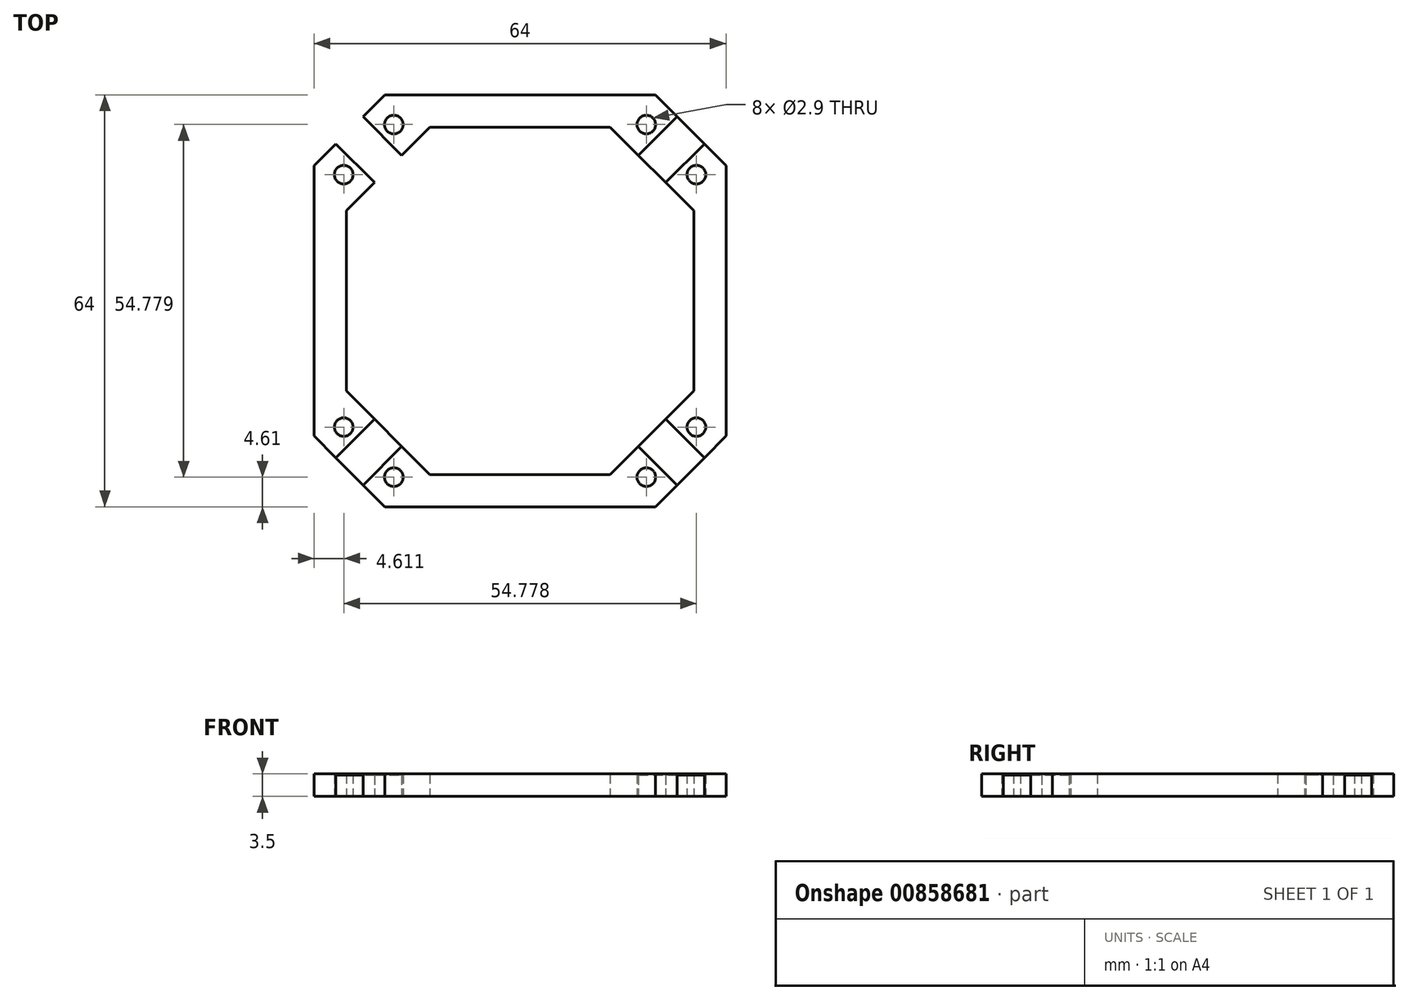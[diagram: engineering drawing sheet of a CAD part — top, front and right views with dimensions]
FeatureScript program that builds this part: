
annotation { "Feature Type Name" : "Feature", "Feature Type Description" : "" }
export const myFeature = defineFeature(function(context is Context, id is Id, definition is map)
    precondition{}
    {
        {
            var Q0;
            Q0=qCreatedBy(makeId("Top.planeOp"),FACE);
            var sketch = newSketch(context, id + "F0", { "sketchPlane" : qUnion([Q0])});
            skLineSegment(sketch, "E0.bottom", {"start": v(21, 32) * mm, "end": v(-21, 32) * mm});
            skLineSegment(sketch, "E0.top", {"start": v(21, -32) * mm, "end": v(-21, -32) * mm});
            skLineSegment(sketch, "E0.left", {"start": v(32, 21) * mm, "end": v(32, -21) * mm});
            skLineSegment(sketch, "E0.right", {"start": v(-32, 21) * mm, "end": v(-32, -21) * mm});
            skPoint(sketch, "E0.middle", {"position": v(0, 0) * mm});
            skLineSegment(sketch, "E1.left", {"start": v(27, 14) * mm, "end": v(27, -14) * mm});
            skLineSegment(sketch, "E1.right", {"start": v(-27, 14) * mm, "end": v(-27, -14) * mm});
            skLineSegment(sketch, "E2.bottom", {"start": v(14, 27) * mm, "end": v(-14, 27) * mm});
            skLineSegment(sketch, "E2.top", {"start": v(14, -27) * mm, "end": v(-14, -27) * mm});
            skLineSegment(sketch, "E3", {"start": v(-27, 14) * mm, "end": v(-14, 27) * mm});
            skLineSegment(sketch, "E4", {"start": v(14, 27) * mm, "end": v(27, 14) * mm});
            skLineSegment(sketch, "E5", {"start": v(-27, -14) * mm, "end": v(-14, -27) * mm});
            skLineSegment(sketch, "E6", {"start": v(14, -27) * mm, "end": v(27, -14) * mm});
            skLineSegment(sketch, "E7", {"start": v(-32, 21) * mm, "end": v(-21, 32) * mm});
            skLineSegment(sketch, "E8", {"start": v(-32, -21) * mm, "end": v(-21, -32) * mm});
            skLineSegment(sketch, "E9", {"start": v(21, -32) * mm, "end": v(32, -21) * mm});
            skLineSegment(sketch, "E10", {"start": v(21, 32) * mm, "end": v(32, 21) * mm});
            skLineSegment(sketch, "E11", {"start": v(-32, 21) * mm, "end": v(-28.06, 24.94) * mm});
            skLineSegment(sketch, "E12", {"start": v(-25.62, 21.38) * mm, "end": v(-28.62, 24.38) * mm});
            skLineSegment(sketch, "E13", {"start": v(-28.62, 24.38) * mm, "end": v(-25.62, 21.38) * mm});
            skLineSegment(sketch, "E14", {"start": v(-25.62, 21.38) * mm, "end": v(-22.62, 18.38) * mm});
            skLineSegment(sketch, "E15", {"start": v(-21.38, 25.62) * mm, "end": v(-24.38, 28.62) * mm});
            skLineSegment(sketch, "E16", {"start": v(-24.38, 28.62) * mm, "end": v(-21.38, 25.62) * mm});
            skLineSegment(sketch, "E17", {"start": v(-21.38, 25.62) * mm, "end": v(-18.38, 22.62) * mm});
            skLineSegment(sketch, "E18", {"start": v(21.88, 26.13) * mm, "end": v(18.38, 22.62) * mm});
            skLineSegment(sketch, "E19", {"start": v(18.38, 22.62) * mm, "end": v(24.38, 28.62) * mm});
            skLineSegment(sketch, "E20", {"start": v(25.62, 21.38) * mm, "end": v(22.62, 18.38) * mm});
            skLineSegment(sketch, "E21", {"start": v(22.62, 18.38) * mm, "end": v(28.62, 24.38) * mm});
            skLineSegment(sketch, "E22", {"start": v(-25.62, -21.38) * mm, "end": v(-28.62, -24.38) * mm});
            skLineSegment(sketch, "E23", {"start": v(-28.62, -24.38) * mm, "end": v(-22.62, -18.38) * mm});
            skLineSegment(sketch, "E24", {"start": v(-21.76, -26) * mm, "end": v(-24.38, -28.62) * mm});
            skLineSegment(sketch, "E25", {"start": v(-24.38, -28.62) * mm, "end": v(-18.38, -22.62) * mm});
            skLineSegment(sketch, "E26", {"start": v(20.86, -25.1) * mm, "end": v(18.38, -22.62) * mm});
            skLineSegment(sketch, "E27", {"start": v(18.38, -22.62) * mm, "end": v(24.38, -28.62) * mm});
            skLineSegment(sketch, "E28", {"start": v(25.62, -21.38) * mm, "end": v(22.62, -18.38) * mm});
            skLineSegment(sketch, "E29", {"start": v(22.62, -18.38) * mm, "end": v(28.62, -24.38) * mm});
            skCircle(sketch, "E30", {"center": v(-27.39, 19.61) * mm, "radius": 1.45 * mm});
            skCircle(sketch, "E31", {"center": v(-19.61, 27.39) * mm, "radius": 1.45 * mm});
            skCircle(sketch, "E32", {"center": v(19.61, 27.39) * mm, "radius": 1.45 * mm});
            skCircle(sketch, "E33", {"center": v(27.39, 19.61) * mm, "radius": 1.45 * mm});
            skCircle(sketch, "E34", {"center": v(-27.39, -19.61) * mm, "radius": 1.45 * mm});
            skCircle(sketch, "E35", {"center": v(-19.61, -27.39) * mm, "radius": 1.45 * mm});
            skCircle(sketch, "E36", {"center": v(19.61, -27.39) * mm, "radius": 1.45 * mm});
            skCircle(sketch, "E37", {"center": v(27.39, -19.61) * mm, "radius": 1.45 * mm});
            skSolve(sketch);
        }
        {
            var Q0;
            {var subQ0=sQuery(id+"F0.wireOp",EDGE,"E13");Q0=makeQuery(id+"F0.imprint","IMPRINT",FACE,{"disambiguationData":[TD([[makeQuery(id+"F0.imprint","IMPRINT",EDGE,{"derivedFrom":subQ0}),1.0]])]});}
            var Q1;
            {var subQ0=sQuery(id+"F0.wireOp",EDGE,"E19");var subQ3=makeQuery(id+"F0.imprint","IMPRINT",VERTEX,{"derivedFrom":subQ0});Q1=makeQuery(id+"F0.imprint","IMPRINT",FACE,{"disambiguationData":[TD([[makeQuery(id+"F0.imprint","IMPRINT",EDGE,{"disambiguationData":[TD([[subQ3,1.0]])],"derivedFrom":subQ0}),-1.0]])]});}
            var Q2;
            {var subQ0=sQuery(id+"F0.wireOp",EDGE,"E27");var subQ3=makeQuery(id+"F0.imprint","IMPRINT",VERTEX,{"derivedFrom":subQ0});Q2=makeQuery(id+"F0.imprint","IMPRINT",FACE,{"disambiguationData":[TD([[makeQuery(id+"F0.imprint","IMPRINT",EDGE,{"disambiguationData":[TD([[subQ3,1.0]])],"derivedFrom":subQ0}),1.0]])]});}
            var Q3;
            {var subQ0=sQuery(id+"F0.wireOp",EDGE,"E23");var subQ3=makeQuery(id+"F0.imprint","IMPRINT",VERTEX,{"derivedFrom":subQ0});Q3=makeQuery(id+"F0.imprint","IMPRINT",FACE,{"disambiguationData":[TD([[makeQuery(id+"F0.imprint","IMPRINT",EDGE,{"disambiguationData":[TD([[subQ3,1.0]])],"derivedFrom":subQ0}),-1.0]])]});}
            extrude(context, id + "F1", {"entities" : qUnion([Q0, Q1, Q2, Q3]), "depth" : 3.3 * mm, "offsetDistance" : 25 * mm});
        }
        {
            var Q0;
            {var subQ10=sQuery(id+"F0.wireOp",EDGE,"E0.top");Q0=makeQuery(id+"F0.imprint","IMPRINT",FACE,{"disambiguationData":[TD([[makeQuery(id+"F0.imprint","IMPRINT",EDGE,{"derivedFrom":subQ10}),-1.0]])]});}
            var Q1;
            {var subQ6=sQuery(id+"F0.wireOp",EDGE,"E0.right");Q1=makeQuery(id+"F0.imprint","IMPRINT",FACE,{"disambiguationData":[TD([[makeQuery(id+"F0.imprint","IMPRINT",EDGE,{"derivedFrom":subQ6}),1.0]])]});}
            var Q2;
            {var subQ6=sQuery(id+"F0.wireOp",EDGE,"E0.bottom");Q2=makeQuery(id+"F0.imprint","IMPRINT",FACE,{"disambiguationData":[TD([[makeQuery(id+"F0.imprint","IMPRINT",EDGE,{"derivedFrom":subQ6}),1.0]])]});}
            var Q3;
            {var subQ13=sQuery(id+"F0.wireOp",EDGE,"E0.left");Q3=makeQuery(id+"F0.imprint","IMPRINT",FACE,{"disambiguationData":[TD([[makeQuery(id+"F0.imprint","IMPRINT",EDGE,{"derivedFrom":subQ13}),-1.0]])]});}
            extrude(context, id + "F2", {"entities" : qUnion([Q0, Q1, Q2, Q3]), "depth" : 3.5 * mm, "offsetDistance" : 25 * mm});
        }
    });
